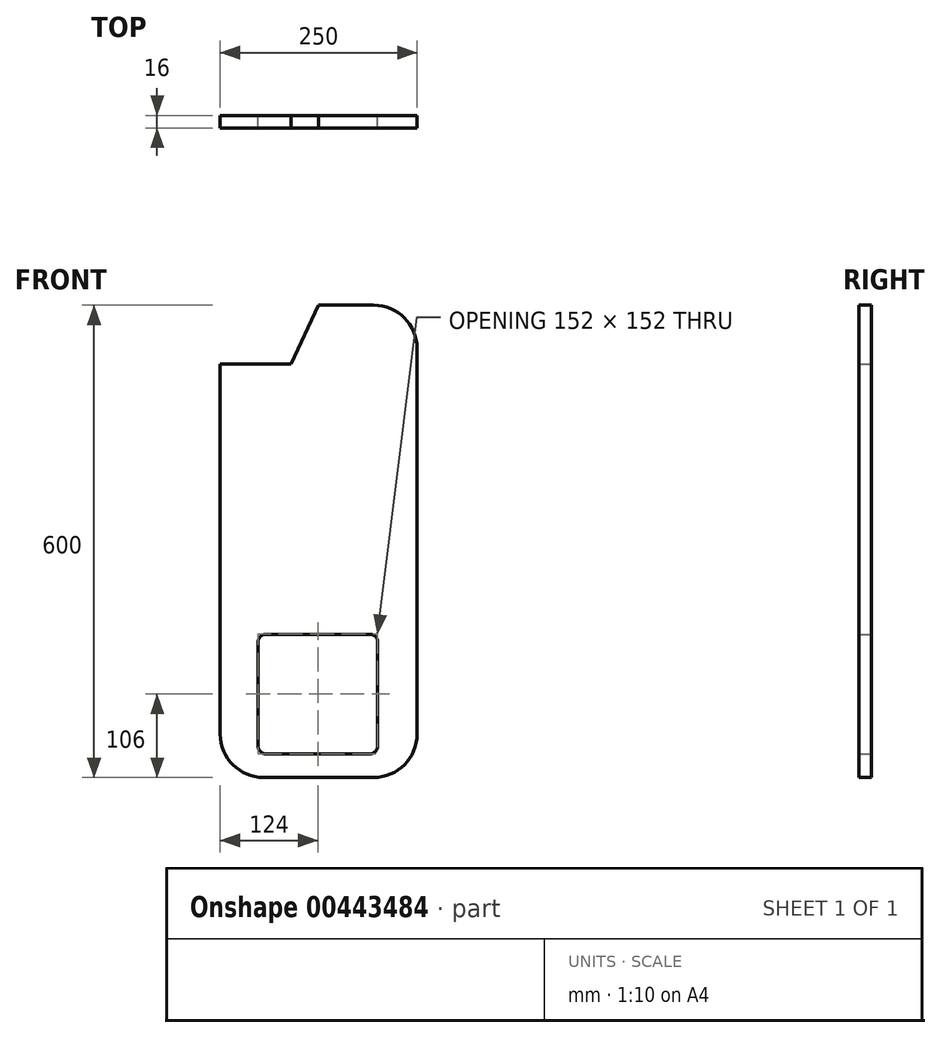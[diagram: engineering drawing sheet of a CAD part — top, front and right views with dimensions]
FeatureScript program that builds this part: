
annotation { "Feature Type Name" : "Feature", "Feature Type Description" : "" }
export const myFeature = defineFeature(function(context is Context, id is Id, definition is map)
    precondition{}
    {
        {
            var Q0;
            Q0=qCreatedBy(makeId("Front.planeOp"),FACE);
            var sketch = newSketch(context, id + "F0", { "sketchPlane" : qUnion([Q0])});
            skLineSegment(sketch, "E0.bottom", {"start": v(55, 0) * mm, "end": v(195, 0) * mm});
            skLineSegment(sketch, "E0.top", {"start": v(0, 600) * mm, "end": v(195, 600) * mm});
            skLineSegment(sketch, "E0.left", {"start": v(0, 55) * mm, "end": v(0, 600) * mm});
            skLineSegment(sketch, "E0.right", {"start": v(250, 55) * mm, "end": v(250, 545) * mm});
            skLineSegment(sketch, "E1.bottom", {"start": v(58, 182) * mm, "end": v(190, 182) * mm});
            skLineSegment(sketch, "E1.top", {"start": v(58, 30) * mm, "end": v(190, 30) * mm});
            skLineSegment(sketch, "E1.left", {"start": v(48, 172) * mm, "end": v(48, 40) * mm});
            skLineSegment(sketch, "E1.right", {"start": v(200, 172) * mm, "end": v(200, 40) * mm});
            skLineSegment(sketch, "E2", {"start": v(0, 525) * mm, "end": v(90, 525) * mm});
            skLineSegment(sketch, "E3", {"start": v(90, 525) * mm, "end": v(125, 600) * mm});
            skPoint(sketch, "E4.visualSharp", {"position": v(250, 0) * mm});
            skArc(sketch, "E4.filletArc", {"start": v(195, 0) * mm, "mid": v(233.9, 16.1) * mm, "end": v(250, 55) * mm});
            skPoint(sketch, "E5.visualSharp", {"position": v(0, 0) * mm});
            skArc(sketch, "E5.filletArc", {"start": v(0, 55) * mm, "mid": v(16.1, 16.1) * mm, "end": v(55, 0) * mm});
            skPoint(sketch, "E6.visualSharp", {"position": v(250, 600) * mm});
            skArc(sketch, "E6.filletArc", {"start": v(250, 545) * mm, "mid": v(233.9, 583.9) * mm, "end": v(195, 600) * mm});
            skPoint(sketch, "E7.visualSharp", {"position": v(48, 182) * mm});
            skArc(sketch, "E7.filletArc", {"start": v(58, 182) * mm, "mid": v(50.93, 179.07) * mm, "end": v(48, 172) * mm});
            skPoint(sketch, "E8.visualSharp", {"position": v(200, 182) * mm});
            skArc(sketch, "E8.filletArc", {"start": v(200, 172) * mm, "mid": v(197.07, 179.07) * mm, "end": v(190, 182) * mm});
            skPoint(sketch, "E9.visualSharp", {"position": v(200, 30) * mm});
            skArc(sketch, "E9.filletArc", {"start": v(190, 30) * mm, "mid": v(197.07, 32.93) * mm, "end": v(200, 40) * mm});
            skPoint(sketch, "E10.visualSharp", {"position": v(48, 30) * mm});
            skArc(sketch, "E10.filletArc", {"start": v(48, 40) * mm, "mid": v(50.93, 32.93) * mm, "end": v(58, 30) * mm});
            skSolve(sketch);
        }
        {
            var Q0;
            Q0=makeQuery(id+"F0.imprint","IMPRINT",FACE,{"disambiguationData":[TD([[makeQuery(id+"F0.imprint","IMPRINT",EDGE,{"derivedFrom":sQuery(id+"F0.wireOp",EDGE,"E0.bottom")}),1.0]])]});
            extrude(context, id + "F1", {"entities" : qUnion([Q0]), "depth" : 16 * mm});
        }
    });
